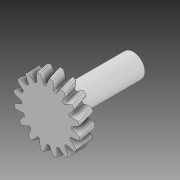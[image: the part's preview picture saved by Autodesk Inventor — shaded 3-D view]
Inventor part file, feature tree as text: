
AUTODESK INVENTOR PART (.ipt)
format: ipt  version: 2020 (Build 240168000, 168)  size: 421,376 bytes
history: native  units: mm
features: other x2, sketch x2, revolve x1, extrude x1
ambient origin geometry x8: Origin, YZ Plane, XZ Plane, XY Plane, X Axis, Y Axis, Z Axis, Center Point
bodies: Solid1 (feature_tree)
feature tree (6):
  revolve  "Revolution1"  [1 undecoded]
  other  "Spur Gear Teeth1"
  extrude  "Extrusion1"  Depth=22.0mm
  sketch  "Sketch1"  dims[d0=3.9mm d1=2.0mm]
  other  "Spur Gear1"
  sketch  "Sketch2"  dims[d2=1.0mm d3=22.0mm d4=5.0mm d5=15.0mm d7=90.0deg d8=6.45mm d9=3.0mm d10=0.0mm]
note: 1 required parameter value undecoded (feature->parameter linkage not recoverable at this tier; creation-order binding heuristic only, values carry confidence <= 0.55)
